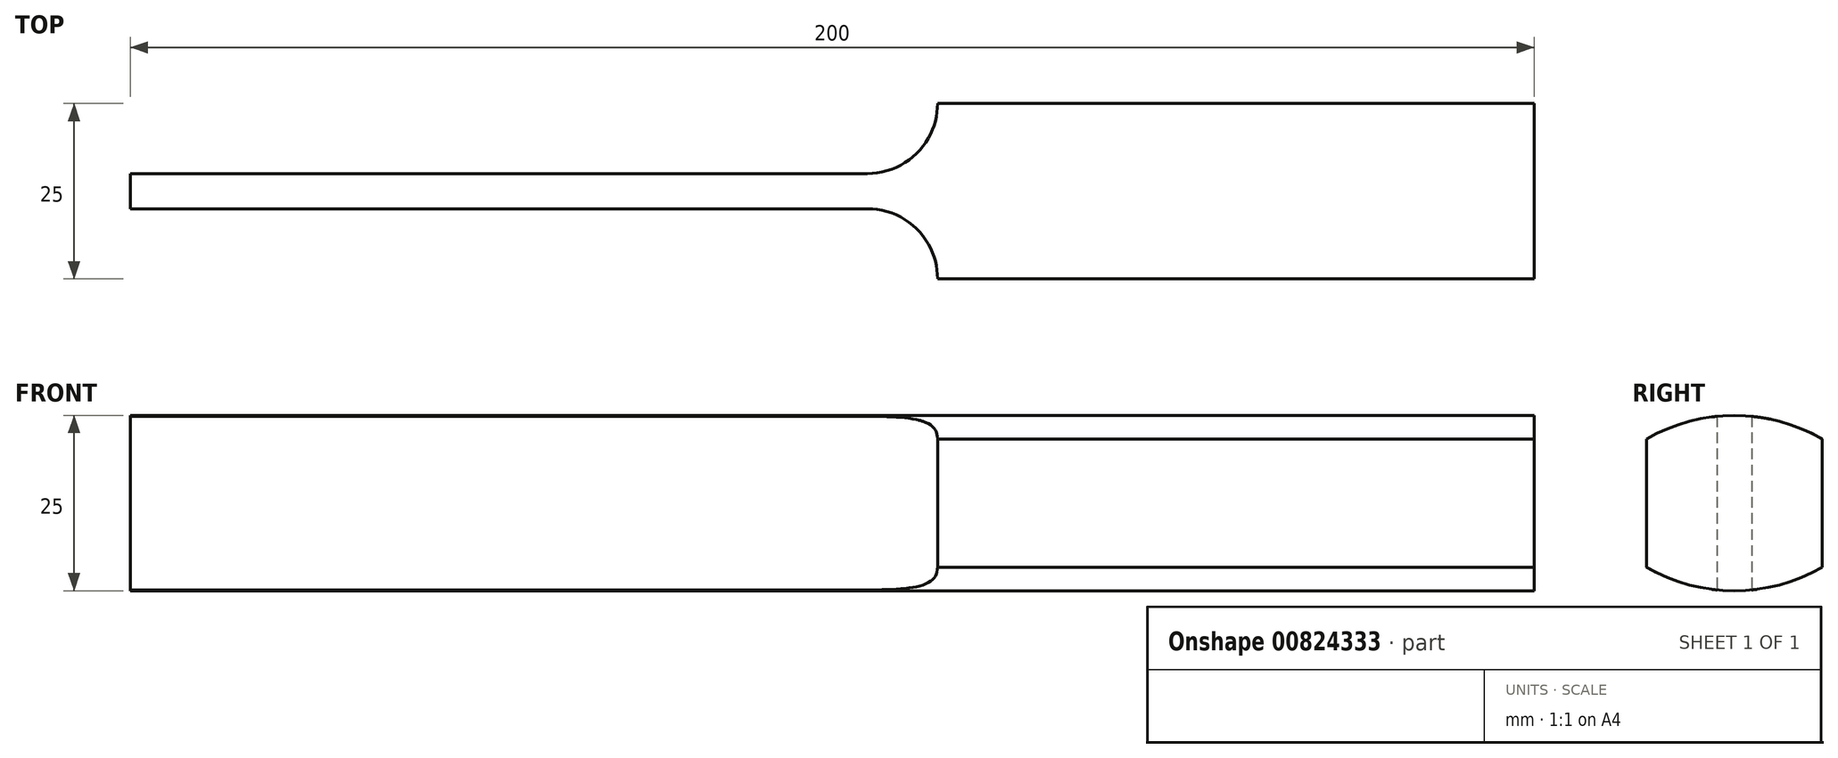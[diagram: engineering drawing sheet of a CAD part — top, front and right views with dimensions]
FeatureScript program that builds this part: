
annotation { "Feature Type Name" : "Feature", "Feature Type Description" : "" }
export const myFeature = defineFeature(function(context is Context, id is Id, definition is map)
    precondition{}
    {
        {
            var Q0;
            Q0=qCreatedBy(makeId("Top.planeOp"),FACE);
            var sketch = newSketch(context, id + "F0", { "sketchPlane" : qUnion([Q0])});
            skLineSegment(sketch, "E0.bottom", {"start": v(100, -12.5) * mm, "end": v(-100, -12.5) * mm});
            skLineSegment(sketch, "E0.top", {"start": v(100, 12.5) * mm, "end": v(-100, 12.5) * mm});
            skLineSegment(sketch, "E0.left", {"start": v(100, -12.5) * mm, "end": v(100, 12.5) * mm});
            skLineSegment(sketch, "E0.right", {"start": v(-100, -12.5) * mm, "end": v(-100, 12.5) * mm});
            skPoint(sketch, "E0.middle", {"position": v(0, 0) * mm});
            skSolve(sketch);
        }
        {
            var Q0;
            Q0=makeQuery(id+"F0.imprint","IMPRINT",FACE,{"disambiguationData":[TD([[makeQuery(id+"F0.imprint","IMPRINT",EDGE,{"derivedFrom":sQuery(id+"F0.wireOp",EDGE,"E0.bottom")}),-1.0]])]});
            extrude(context, id + "F1", {"entities" : qUnion([Q0]), "depth" : 25 * mm, "offsetDistance" : 25 * mm});
        }
        {
            var Q0;
            Q0=makeQuery(id+"F1.opExtrude","SWEPT_FACE",FACE,{"disambiguationData":[OSD([sQuery(id+"F0.wireOp",EDGE,"E0.left")])]});
            var sketch = newSketch(context, id + "F2", { "sketchPlane" : qUnion([Q0])});
            skPoint(sketch, "E1.0", {"position": v(0, 0) * mm});
            skLineSegment(sketch, "E2", {"start": v(0, 0) * mm, "end": v(0, 36.7) * mm, "construction": true});
            skCircle(sketch, "E3", {"center": v(0, 0) * mm, "radius": 25 * mm});
            skCircle(sketch, "E4", {"center": v(0, 25) * mm, "radius": 25 * mm});
            skSolve(sketch);
        }
        {
            var Q0;
            {var subQ0=sQuery(id+"F2.wireOp",EDGE,"E3");var subQ1=sQuery(id+"F0.wireOp",EDGE,"E0.left");var subQ2=makeQuery(id+"F1.opExtrude","CAP_EDGE",EDGE,{"disambiguationData":[OSD([subQ1])],"isStart":false});var subQ3=makeQuery(id+"F2.imprint","INTERSECT",VERTEX,{"derivedFrom":[subQ2,subQ0]});Q0=makeQuery(id+"F2.imprint","IMPRINT",FACE,{"disambiguationData":[TD([[makeQuery(id+"F2.imprint","IMPRINT",EDGE,{"disambiguationData":[TD([[subQ3,-1.0]])],"derivedFrom":subQ0}),-1.0]])]});}
            var Q1;
            {var subQ0=sQuery(id+"F2.wireOp",EDGE,"E3");var subQ1=sQuery(id+"F0.wireOp",EDGE,"E0.left");var subQ4=makeQuery(id+"F1.opExtrude","CAP_EDGE",EDGE,{"disambiguationData":[OSD([subQ1])],"isStart":false});var subQ5=makeQuery(id+"F2.imprint","INTERSECT",VERTEX,{"derivedFrom":[subQ4,subQ0]});Q1=makeQuery(id+"F2.imprint","IMPRINT",FACE,{"disambiguationData":[TD([[makeQuery(id+"F2.imprint","IMPRINT",EDGE,{"disambiguationData":[TD([[subQ5,1.0]])],"derivedFrom":subQ0}),-1.0]])]});}
            var Q2;
            {var subQ0=sQuery(id+"F2.wireOp",EDGE,"E4");var subQ1=sQuery(id+"F0.wireOp",EDGE,"E0.left");var subQ4=makeQuery(id+"F1.opExtrude","CAP_EDGE",EDGE,{"disambiguationData":[OSD([subQ1])],"isStart":true});var subQ5=makeQuery(id+"F2.imprint","INTERSECT",VERTEX,{"derivedFrom":[subQ4,subQ0]});Q2=makeQuery(id+"F2.imprint","IMPRINT",FACE,{"disambiguationData":[TD([[makeQuery(id+"F2.imprint","IMPRINT",EDGE,{"disambiguationData":[TD([[subQ5,1.0]])],"derivedFrom":subQ0}),-1.0]])]});}
            var Q3;
            {var subQ0=sQuery(id+"F2.wireOp",EDGE,"E4");var subQ1=sQuery(id+"F0.wireOp",EDGE,"E0.left");var subQ2=makeQuery(id+"F1.opExtrude","CAP_EDGE",EDGE,{"disambiguationData":[OSD([subQ1])],"isStart":true});var subQ3=makeQuery(id+"F2.imprint","INTERSECT",VERTEX,{"derivedFrom":[subQ2,subQ0]});Q3=makeQuery(id+"F2.imprint","IMPRINT",FACE,{"disambiguationData":[TD([[makeQuery(id+"F2.imprint","IMPRINT",EDGE,{"disambiguationData":[TD([[subQ3,-1.0]])],"derivedFrom":subQ0}),-1.0]])]});}
            extrude(context, id + "F3", {"entities" : qUnion([Q0, Q1, Q2, Q3]), "operationType" : NewBodyOperationType.REMOVE, "endBound" : BoundingType.THROUGH_ALL, "oppositeDirection" : true, "depth" : 25 * mm, "offsetDistance" : 25 * mm});
        }
        {
            var Q0;
            Q0=qCreatedBy(makeId("Top.planeOp"),FACE);
            var sketch = newSketch(context, id + "F4", { "sketchPlane" : qUnion([Q0])});
            skLineSegment(sketch, "E5", {"start": v(-125.72, 0) * mm, "end": v(116.86, 0) * mm, "construction": true});
            skLineSegment(sketch, "E6.0", {"start": v(-100, -12.5) * mm, "end": v(-100, 12.5) * mm});
            skLineSegment(sketch, "E7.bottom", {"start": v(5, -2.5) * mm, "end": v(-100, -2.5) * mm});
            skLineSegment(sketch, "E7.top", {"start": v(5, 2.5) * mm, "end": v(-100, 2.5) * mm});
            skLineSegment(sketch, "E7.right", {"start": v(-100, -2.5) * mm, "end": v(-100, 2.5) * mm});
            skPoint(sketch, "E7.middle", {"position": v(-47.5, 0) * mm});
            skLineSegment(sketch, "E8.0", {"start": v(-100, 12.5) * mm, "end": v(100, 12.5) * mm});
            skLineSegment(sketch, "E9.0", {"start": v(-100, -12.5) * mm, "end": v(100, -12.5) * mm});
            skArc(sketch, "E10", {"start": v(5, 2.5) * mm, "mid": v(12.07, 5.43) * mm, "end": v(15, 12.5) * mm});
            skArc(sketch, "E11", {"start": v(5, -2.5) * mm, "mid": v(12.07, -5.43) * mm, "end": v(15, -12.5) * mm});
            skLineSegment(sketch, "E12", {"start": v(15, 12.5) * mm, "end": v(-100, 12.5) * mm});
            skLineSegment(sketch, "E13", {"start": v(-100, 12.5) * mm, "end": v(-100, 2.5) * mm});
            skLineSegment(sketch, "E14", {"start": v(-100, -2.5) * mm, "end": v(-100, -12.5) * mm});
            skLineSegment(sketch, "E15", {"start": v(-100, -12.5) * mm, "end": v(15, -12.5) * mm});
            skSolve(sketch);
        }
        {
            var Q0;
            Q0 = qSketchRegion(id + "F4", true);
            extrude(context, id + "F5", {"entities" : qUnion([Q0]), "operationType" : NewBodyOperationType.REMOVE, "endBound" : BoundingType.THROUGH_ALL, "depth" : 25 * mm, "offsetDistance" : 25 * mm});
        }
    });
